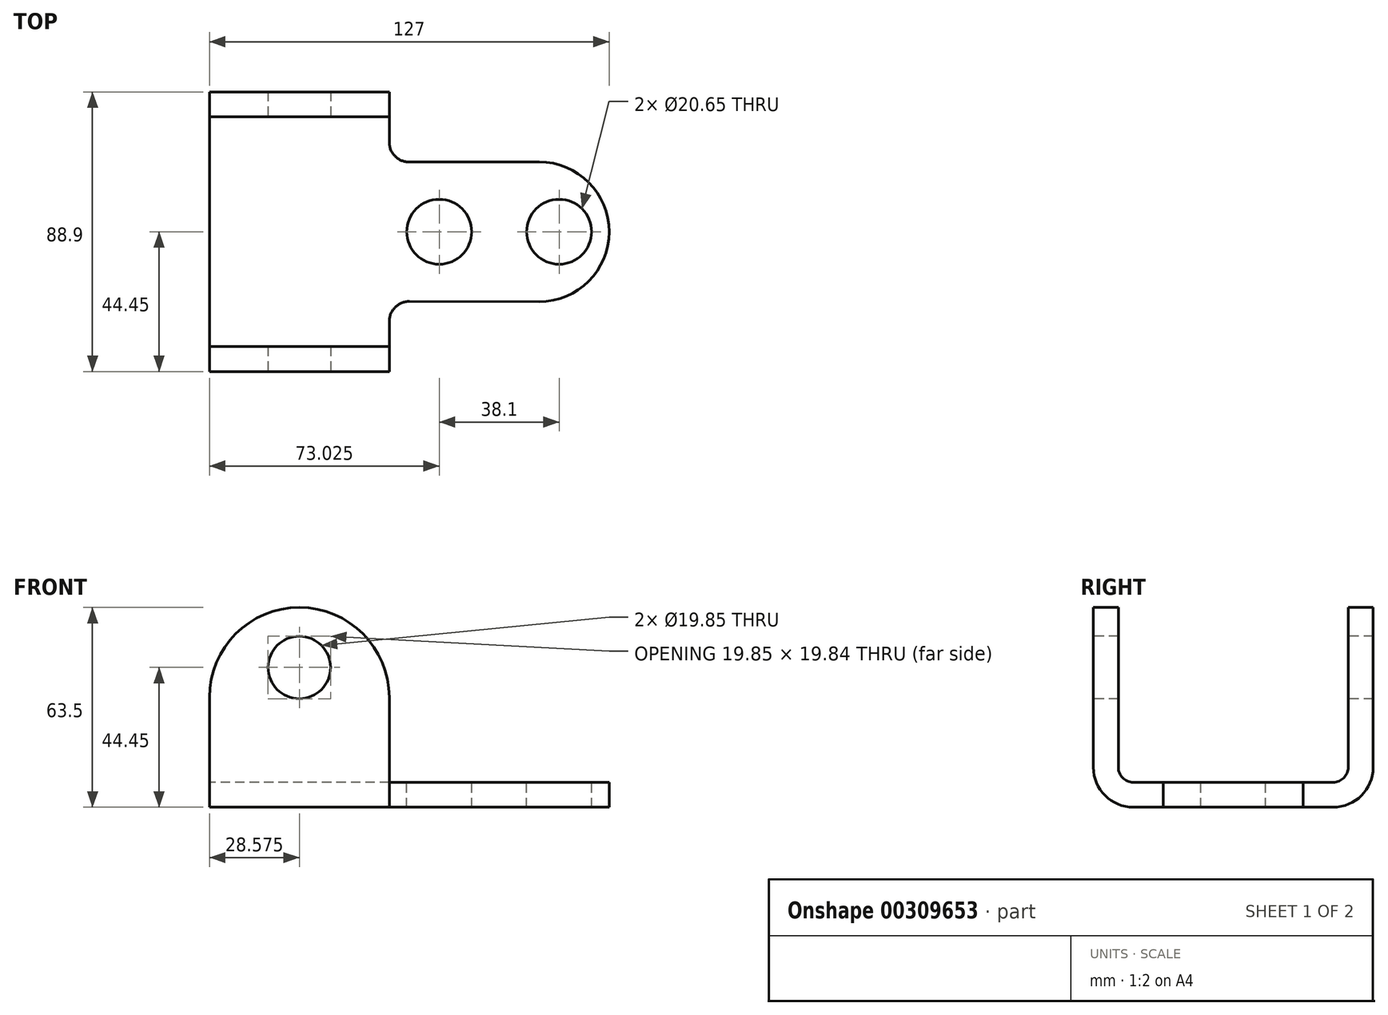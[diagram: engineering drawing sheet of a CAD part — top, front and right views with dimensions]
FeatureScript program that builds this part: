
annotation { "Feature Type Name" : "Feature", "Feature Type Description" : "" }
export const myFeature = defineFeature(function(context is Context, id is Id, definition is map)
    precondition{}
    {
        {
            var Q0;
            Q0=qCreatedBy(makeId("Right.planeOp"),FACE);
            var sketch = newSketch(context, id + "F0", { "sketchPlane" : qUnion([Q0])});
            skLineSegment(sketch, "E0", {"start": v(-12.7, 0) * mm, "end": v(-76.2, 0) * mm});
            skLineSegment(sketch, "E1", {"start": v(-88.9, 12.7) * mm, "end": v(-88.9, 63.5) * mm});
            skLineSegment(sketch, "E2", {"start": v(-88.9, 63.5) * mm, "end": v(-80.96, 63.5) * mm});
            skLineSegment(sketch, "E3", {"start": v(-80.96, 63.5) * mm, "end": v(-80.96, 12.7) * mm});
            skLineSegment(sketch, "E4", {"start": v(-76.2, 7.94) * mm, "end": v(-12.7, 7.94) * mm});
            skLineSegment(sketch, "E5", {"start": v(-7.94, 12.7) * mm, "end": v(-7.94, 63.5) * mm});
            skLineSegment(sketch, "E6", {"start": v(-7.94, 63.5) * mm, "end": v(0, 63.5) * mm});
            skLineSegment(sketch, "E7", {"start": v(0, 63.5) * mm, "end": v(0, 12.7) * mm});
            skPoint(sketch, "E8.visualSharp", {"position": v(0, 0) * mm});
            skArc(sketch, "E8.filletArc", {"start": v(-12.7, 0) * mm, "mid": v(-3.72, 3.72) * mm, "end": v(0, 12.7) * mm});
            skPoint(sketch, "E9.visualSharp", {"position": v(-88.9, 0) * mm});
            skArc(sketch, "E9.filletArc", {"start": v(-88.9, 12.7) * mm, "mid": v(-85.18, 3.72) * mm, "end": v(-76.2, 0) * mm});
            skPoint(sketch, "E10.visualSharp", {"position": v(-7.94, 7.94) * mm});
            skArc(sketch, "E10.filletArc", {"start": v(-12.7, 7.94) * mm, "mid": v(-9.33, 9.33) * mm, "end": v(-7.94, 12.7) * mm});
            skPoint(sketch, "E11.visualSharp", {"position": v(-80.96, 7.94) * mm});
            skArc(sketch, "E11.filletArc", {"start": v(-80.96, 12.7) * mm, "mid": v(-79.57, 9.33) * mm, "end": v(-76.2, 7.94) * mm});
            skSolve(sketch);
        }
        {
            var Q0;
            Q0=makeQuery(id+"F0.imprint","IMPRINT",FACE,{"disambiguationData":[TD([[makeQuery(id+"F0.imprint","IMPRINT",EDGE,{"derivedFrom":sQuery(id+"F0.wireOp",EDGE,"E0")}),-1.0]])]});
            extrude(context, id + "F1", {"entities" : qUnion([Q0]), "depth" : 127 * mm});
        }
        {
            var Q0;
            Q0=makeQuery(id+"F1.opExtrude","SWEPT_FACE",FACE,{"disambiguationData":[OSD([sQuery(id+"F0.wireOp",EDGE,"E1")])]});
            var sketch = newSketch(context, id + "F2", { "sketchPlane" : qUnion([Q0])});
            skLineSegment(sketch, "E12.bottom", {"start": v(28.58, 63.5) * mm, "end": v(28.58, 63.5) * mm});
            skLineSegment(sketch, "E12.top", {"start": v(0, 12.7) * mm, "end": v(57.15, 12.7) * mm});
            skLineSegment(sketch, "E12.left", {"start": v(0, 34.92) * mm, "end": v(0, 12.7) * mm});
            skLineSegment(sketch, "E12.right", {"start": v(57.15, 34.92) * mm, "end": v(57.15, 12.7) * mm});
            skPoint(sketch, "E13.visualSharp", {"position": v(0, 63.5) * mm});
            skArc(sketch, "E13.filletArc", {"start": v(28.58, 63.5) * mm, "mid": v(8.37, 55.13) * mm, "end": v(0, 34.92) * mm});
            skPoint(sketch, "E14.visualSharp", {"position": v(57.15, 63.5) * mm});
            skArc(sketch, "E14.filletArc", {"start": v(57.15, 34.92) * mm, "mid": v(48.78, 55.13) * mm, "end": v(28.58, 63.5) * mm});
            skLineSegment(sketch, "E15", {"start": v(0, 34.92) * mm, "end": v(0, 63.5) * mm});
            skLineSegment(sketch, "E16", {"start": v(28.58, 63.5) * mm, "end": v(57.15, 63.5) * mm});
            skLineSegment(sketch, "E17", {"start": v(57.15, 34.92) * mm, "end": v(57.15, 63.5) * mm});
            skLineSegment(sketch, "E18", {"start": v(0, 63.5) * mm, "end": v(57.15, 63.5) * mm});
            skSolve(sketch);
        }
        {
            var Q0;
            {var subQ0=sQuery(id+"F2.wireOp",EDGE,"E13.filletArc");Q0=makeQuery(id+"F2.imprint","IMPRINT",FACE,{"disambiguationData":[TD([[makeQuery(id+"F2.imprint","IMPRINT",EDGE,{"derivedFrom":subQ0}),-1.0]])]});}
            var Q1;
            {var subQ0=sQuery(id+"F2.wireOp",EDGE,"E14.filletArc");Q1=makeQuery(id+"F2.imprint","IMPRINT",FACE,{"disambiguationData":[TD([[makeQuery(id+"F2.imprint","IMPRINT",EDGE,{"derivedFrom":subQ0}),-1.0]])]});}
            extrude(context, id + "F3", {"entities" : qUnion([Q0, Q1]), "operationType" : NewBodyOperationType.REMOVE, "endBound" : BoundingType.THROUGH_ALL, "oppositeDirection" : true, "depth" : 25.4 * mm});
        }
        {
            var Q0;
            Q0=makeQuery(id+"F1.opExtrude","SWEPT_FACE",FACE,{"disambiguationData":[OSD([sQuery(id+"F0.wireOp",EDGE,"E6")])]});
            var sketch = newSketch(context, id + "F4", { "sketchPlane" : qUnion([Q0])});
            skLineSegment(sketch, "E19", {"start": v(57.15, 0) * mm, "end": v(57.15, -15.95) * mm});
            skLineSegment(sketch, "E20", {"start": v(57.15, -72.95) * mm, "end": v(57.15, -88.9) * mm});
            skArc(sketch, "E21", {"start": v(104.77, -66.67) * mm, "mid": v(127, -44.45) * mm, "end": v(104.77, -22.22) * mm});
            skLineSegment(sketch, "E22", {"start": v(104.77, -22.22) * mm, "end": v(63.51, -22.3) * mm});
            skLineSegment(sketch, "E23", {"start": v(104.77, -66.67) * mm, "end": v(63.51, -66.6) * mm});
            skPoint(sketch, "E24.visualSharp", {"position": v(57.15, -22.3) * mm});
            skArc(sketch, "E24.filletArc", {"start": v(57.15, -15.95) * mm, "mid": v(59.01, -20.44) * mm, "end": v(63.51, -22.3) * mm});
            skPoint(sketch, "E25.visualSharp", {"position": v(57.15, -66.6) * mm});
            skArc(sketch, "E25.filletArc", {"start": v(63.51, -66.6) * mm, "mid": v(59.01, -68.46) * mm, "end": v(57.15, -72.95) * mm});
            skLineSegment(sketch, "E26", {"start": v(57.15, 0) * mm, "end": v(127, 0) * mm});
            skLineSegment(sketch, "E27", {"start": v(127, 0) * mm, "end": v(127, -88.9) * mm});
            skPoint(sketch, "E27.endSnap0", {"position": v(127, -44.45) * mm});
            skLineSegment(sketch, "E28", {"start": v(57.15, -88.9) * mm, "end": v(127, -88.9) * mm});
            skSolve(sketch);
        }
        {
            var Q0;
            Q0 = qSketchRegion(id + "F4", true);
            extrude(context, id + "F5", {"entities" : qUnion([Q0]), "operationType" : NewBodyOperationType.REMOVE, "endBound" : BoundingType.THROUGH_ALL, "oppositeDirection" : true, "depth" : 25.4 * mm});
        }
        {
            var Q0;
            Q0=makeQuery(id+"F1.opExtrude","SWEPT_FACE",FACE,{"disambiguationData":[OSD([sQuery(id+"F0.wireOp",EDGE,"E1")])]});
            var sketch = newSketch(context, id + "F6", { "sketchPlane" : qUnion([Q0])});
            skCircle(sketch, "E29", {"center": v(28.58, 44.45) * mm, "radius": 9.92 * mm});
            skLineSegment(sketch, "E30", {"start": v(0, 0) * mm, "end": v(57.15, 0) * mm});
            skSolve(sketch);
        }
        {
            var Q0;
            Q0 = qSketchRegion(id + "F6", true);
            extrude(context, id + "F7", {"entities" : qUnion([Q0]), "operationType" : NewBodyOperationType.REMOVE, "endBound" : BoundingType.THROUGH_ALL, "oppositeDirection" : true, "depth" : 25.4 * mm});
        }
        {
            var Q0;
            Q0=makeQuery(id+"F1.opExtrude","SWEPT_FACE",FACE,{"disambiguationData":[OSD([sQuery(id+"F0.wireOp",EDGE,"E4")])]});
            var sketch = newSketch(context, id + "F8", { "sketchPlane" : qUnion([Q0])});
            skCircle(sketch, "E31", {"center": v(73.03, -44.45) * mm, "radius": 10.33 * mm});
            skCircle(sketch, "E32", {"center": v(111.12, -44.45) * mm, "radius": 10.33 * mm});
            skSolve(sketch);
        }
        {
            var Q0;
            Q0=makeQuery(id+"F8.imprint","IMPRINT",FACE,{"disambiguationData":[TD([[makeQuery(id+"F8.imprint","IMPRINT",EDGE,{"derivedFrom":sQuery(id+"F8.wireOp",EDGE,"E31")}),1.0]])]});
            var Q1;
            Q1=makeQuery(id+"F8.imprint","IMPRINT",FACE,{"disambiguationData":[TD([[makeQuery(id+"F8.imprint","IMPRINT",EDGE,{"derivedFrom":sQuery(id+"F8.wireOp",EDGE,"E32")}),1.0]])]});
            extrude(context, id + "F9", {"entities" : qUnion([Q0, Q1]), "operationType" : NewBodyOperationType.REMOVE, "oppositeDirection" : true, "depth" : 25.4 * mm});
        }
    });
